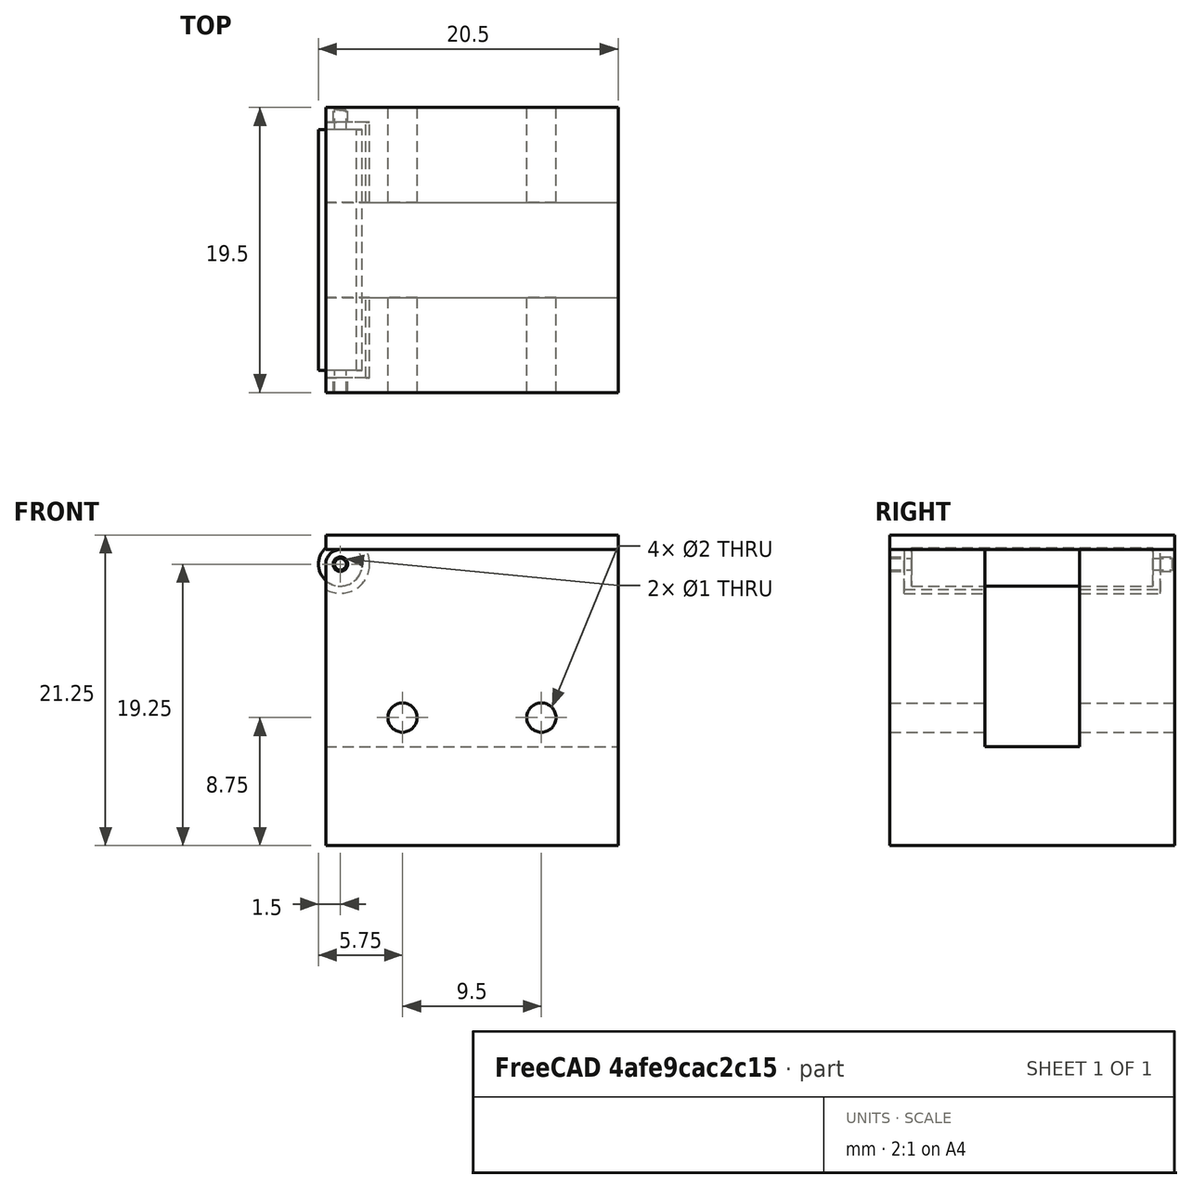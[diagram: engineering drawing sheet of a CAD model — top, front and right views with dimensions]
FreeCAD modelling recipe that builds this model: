
FCSTD DOCUMENT  (FreeCAD 0.17R13541 (Git))
Label: cnc_z_axis_limit
License: All rights reserved
LicenseURL: http://en.wikipedia.org/wiki/All_rights_reserved
objects: Part::Cylinder×6, Part::MultiFuse×4, Part::Box×3, Part::Cut×3, Part::Fillet×1, Part::Cone×1, Part::MultiCommon×1, Spreadsheet::Sheet×1
note: 19 computed .brp shape members not serialized (recipe doc carries the construction recipe); baked Part::Feature solids carry a one-line shape summary decoded from their .brp

FEATURE [Part::Box] Box  label="main_block"
  AttacherType = Attacher::AttachEngine3D
  Height = 20.25
  Length = 20
  Placement = pos=(0,-6.5,-6.75) rot=(0,0,1;0rad)
  Width = 19.5
  expr: Placement.Base.z = -(Height - Switch_Dimensions.Height)
  expr: Height = Switch_Dimensions.Height * 1.5
  expr: Placement.Base.y = -(Width / 3)
  expr: Width = Switch_Dimensions.Width * 3
  expr: Length = Switch_Dimensions.Length
FEATURE [Part::Box] Box001  label="Switch"
  AttacherType = Attacher::AttachEngine3D
  Height = 13.5
  Length = 20
  Width = 6.5
  expr: Width = Switch_Dimensions.Width
  expr: Height = Switch_Dimensions.Height
  expr: Length = Switch_Dimensions.Length
FEATURE [Part::Cylinder] Cylinder  label="main_block_hinge_notch"
  Angle = 360
  AttacherType = Attacher::AttachEngine3D
  Height = 17.5
  Placement = pos=(1,-5.5,12.5) rot=(-1,0,0;1.5708rad)
  Radius = 2
  expr: Placement.Base.y = -(Switch_Dimensions.Width - Radius / 2)
  expr: Radius = main_block.Length / 10
  expr: Placement.Base.z = main_block.Height + main_block.Placement.Base.z - Radius / 2
  expr: Placement.Base.x = Radius / 2
  expr: Height = main_block.Width - 2mm
FEATURE [Part::Cut] Cut
  Base = -> Box
  Tool = -> Cylinder
FEATURE [Part::Cylinder] Cylinder001  label="Hinge_pin_hole"
  Angle = 360
  AttacherType = Attacher::AttachEngine3D
  Height = 19.5
  Placement = pos=(1,-6.5,12.5) rot=(-1,0,0;1.5708rad)
  Radius = 0.5
  expr: Radius = main_block_hinge_notch.Radius / 4
  expr: Placement.Base.y = main_block.Placement.Base.y
  expr: Placement.Base.x = Radius * 2
  expr: Height = main_block.Width
  expr: Placement.Base.z = main_block.Height + main_block.Placement.Base.z - main_block_hinge_notch.Radius / 2
FEATURE [Part::Box] Box002  label="lid_body"
  AttacherType = Attacher::AttachEngine3D
  Height = 1
  Length = 20
  Placement = pos=(0,-6.5,13.5) rot=(0,0,1;0rad)
  Width = 19.5
  expr: Placement.Base.z = main_block.Placement.Base.z + main_block.Height
  expr: Placement.Base.x = main_block.Placement.Base.x
  expr: Placement.Base.y = main_block.Placement.Base.y
  expr: Width = main_block.Width
  expr: Length = main_block.Length
FEATURE [Part::Cylinder] Cylinder002  label="lid_hinge_body"
  Angle = 360
  AttacherType = Attacher::AttachEngine3D
  Height = 16.5
  Placement = pos=(1,-5,12.5) rot=(-1,0,0;1.5708rad)
  Radius = 1.5
  expr: Placement.Base.y = main_block_hinge_notch.Placement.Base.y + (main_block_hinge_notch.Height - Height) / 2
  expr: Placement.Base.z = main_block_hinge_notch.Placement.Base.z
  expr: Placement.Base.x = main_block_hinge_notch.Placement.Base.x
  expr: Height = main_block_hinge_notch.Height - 1mm
  expr: Radius = main_block_hinge_notch.Radius - 0.5mm
FEATURE [Part::Cylinder] Cylinder003  label="lid_hinge_pin"
  Angle = 360
  AttacherType = Attacher::AttachEngine3D
  Height = 19.5
  Placement = pos=(1,-6.5,12.5) rot=(-1,0,0;1.5708rad)
  Radius = 0.4
  expr: Placement.Base.y = main_block.Placement.Base.y
  expr: Placement.Base.z = main_block_hinge_notch.Placement.Base.z
  expr: Placement.Base.x = main_block_hinge_notch.Placement.Base.x
  expr: Height = main_block.Width
  expr: Radius = Hinge_pin_hole.Radius - 0.10000000000000001mm
FEATURE [Part::Cylinder] Cylinder004  label="switch_pin_1"
  Angle = 360
  AttacherType = Attacher::AttachEngine3D
  Height = 19.5
  Placement = pos=(5.25,-6.5,2) rot=(-1,0,0;1.5708rad)
  Radius = 1
  expr: Radius = Switch_Dimensions.Hole_Diameter / 2
  expr: Placement.Base.z = Switch_Dimensions.Hole_Height
  expr: Placement.Base.y = main_block.Placement.Base.y
  expr: Placement.Base.x = (Switch_Dimensions.Length - Switch_Dimensions.Hole_Seperation) / 2
  expr: Height = main_block.Width
FEATURE [Part::Cylinder] Cylinder005  label="switch_pin_2"
  Angle = 360
  AttacherType = Attacher::AttachEngine3D
  Height = 19.5
  Placement = pos=(14.75,-6.5,2) rot=(-1,0,0;1.5708rad)
  Radius = 1
  expr: Placement.Base.z = Switch_Dimensions.Hole_Height
  expr: Radius = switch_pin_1.Radius
  expr: Placement.Base.y = switch_pin_1.Placement.Base.y
  expr: Height = switch_pin_1.Height
  expr: Placement.Base.x = switch_pin_1.Placement.Base.x + Switch_Dimensions.Hole_Seperation
FEATURE [Part::MultiFuse] Fusion001
  Shapes = -> [Box001,Cylinder004]
FEATURE [Part::MultiFuse] Fusion002  label="Switch_with_mounting_hole_cutouts"
  Shapes = -> [Fusion001,Cylinder005]
FEATURE [Part::Cut] Cut001
  Base = -> Cut
  Tool = -> Fusion002
FEATURE [Part::Cut] Cut002
  Base = -> Cut001
  Tool = -> Cylinder001
FEATURE [Part::Fillet] Fillet
  Base = -> Cut002
  Edges = 2 edges r=1: [Edge1,Edge9]
FEATURE [Part::Cone] Cone
  Angle = 360
  AttacherType = Attacher::AttachEngine3D
  Height = 30
  Placement = pos=(0,3,12) rot=(0,1,0;1.5708rad)
  Radius1 = 10
  Radius2 = 6
FEATURE [Part::MultiCommon] Common  label="lid_hinge_pin_tapered"
  Shapes = -> [Cylinder003,Cone]
FEATURE [Part::MultiFuse] Fusion003  label="lid_hinge"
  Shapes = -> [Cylinder002,Common]
FEATURE [Part::MultiFuse] Fusion  label="Lid"
  Shapes = -> [Box002,Fusion003]
FEATURE [Spreadsheet::Sheet] Spreadsheet  label="Switch_Dimensions"
  cells = A1(Length)==20mm; A2(Height)==13.5mm; A3(Width)==6.5mm; A4(Hole_Seperation)==9.5mm; A5(Hole_Diameter)==2mm; A6==2mm
